# Revit family: Zumtobel MELLOW LIGHT 6 inf - EB
name_source: partatom
category: Lighting Fixtures
revit_build: Autodesk Revit 2014 (Build: 20140709_2115(x64)
units: mm (PartAtom-declared; Revit-internal decimal feet)

## types (12) — shared parameters
Assembly Code = D5020200
Body = Zumtobel_Metal_White
Color Filter = 16777215
Cover = Zumtobel_Metal_Aluminium
Description = Mellow light recessed luminaire
Dimming Lamp Color Temperature Shift = <None>
Emit Shape Visible in Rendering = No
Lamp = LED
Manufacturer = Zumtobel Lighting
Tilt Angle = 90.00°
Voltage = 230 V
Wings = Zumtobel_PMMA_White
zero-valued in all types: Default Elevation

## per-type parameters (varying)
| type | Apparent Load | Emit from Rectangle Length | Emit from Rectangle Width | Height | Length | Middle Part | Model | Photometric Web File | URL | Width |
| ML inf EL LED3600 M625 Q | 33 VA | 599 mm | 599 mm | 77 mm  [stored 0.252625 ft] | 623 mm  [stored 2.04396 ft] | Zumtobel_PMMA_White | 42185201 | D37856AA_MLinf_EL_LED3600-840_M625Q_complete.ies | http://www.zumtobel.com
42184948 | 623 mm  [stored 2.04396 ft] |
| ML inf EL LED3600 M625 L | 33 VA | 1224 mm  [stored 4.01575 ft] | 286 mm  [stored 0.93832 ft] | 82 mm  [stored 0.269029 ft] | 1248 mm  [stored 4.09449 ft] | Zumtobel_PMMA_White | 42185202 | D37805AA_MLinf_EL_LED3600-840_M625L12_complete.ies | http://www.zumtobel.com
42184948 | 310 mm  [stored 1.01706 ft] |
| ML inf EL LED3600 M600 Q | 33 VA | 574 mm  [stored 1.8832 ft] | 574 mm  [stored 1.8832 ft] | 77 mm  [stored 0.252625 ft] | 598 mm  [stored 1.96194 ft] | Zumtobel_PMMA_White | 42184770 | D37856AA_MLinf_EL_LED3600-840_M600Q_complete.ies | http://www.zumtobel.com
42184948 | 598 mm  [stored 1.96194 ft] |
| ML inf EL LED3600 M600 L | 34 VA | 1174 mm  [stored 3.85171 ft] | 274 mm  [stored 0.89895 ft] | 82 mm  [stored 0.269029 ft] | 1198 mm  [stored 3.93045 ft] | Zumtobel_PMMA_White | 42184954 | D37805AA_MLinf_EL_LED3600-840_M600L12_complete.ies | http://www.zumtobel.com
42184948 | 298 mm  [stored 0.97769 ft] |
| ML inf EA LED4800 M625 Q | 49 VA | 599 mm | 599 mm | 77 mm  [stored 0.252625 ft] | 623 mm  [stored 2.04396 ft] | Zumtobel_PMMA_White_Diffusor | 42184948 | D37852AA_MLinf_EA_LED4800-840_M625Q_complete.ies | http://www.zumtobel.com
42184948 | 623 mm  [stored 2.04396 ft] |
| ML inf EA LED4800 M625 L | 50 VA | 1224 mm  [stored 4.01575 ft] | 286 mm  [stored 0.93832 ft] | 82 mm  [stored 0.269029 ft] | 1248 mm  [stored 4.09449 ft] | Zumtobel_PMMA_White_Diffusor | 42184949 | D37773AA_MLinf_EA_LED4800-840_M625L12_complete.ies | http://www.zumtobel.com
42182682 | 310 mm  [stored 1.01706 ft] |
| ML inf EA LED4800 M600 Q | 51 VA | 574 mm  [stored 1.8832 ft] | 574 mm  [stored 1.8832 ft] | 77 mm  [stored 0.252625 ft] | 598 mm  [stored 1.96194 ft] | Zumtobel_PMMA_White_Diffusor | 42184769 | D37852AA_MLinf_EA_LED4800-840_M600Q_complete.ies | http://www.zumtobel.com
42182682 | 598 mm  [stored 1.96194 ft] |
| ML inf EA LED4800 M600 L | 50 VA | 1174 mm  [stored 3.85171 ft] | 274 mm  [stored 0.89895 ft] | 82 mm  [stored 0.269029 ft] | 1198 mm  [stored 3.93045 ft] | Zumtobel_PMMA_White_Diffusor | 42184947 | D37773AA_MLinf_EA_LED4800-840_M600L12_complete.ies | http://www.zumtobel.com
42182682 | 298 mm  [stored 0.97769 ft] |
| ML inf EA LED3600 M625 Q | 36 VA | 599 mm | 599 mm | 77 mm  [stored 0.252625 ft] | 623 mm  [stored 2.04396 ft] | Zumtobel_PMMA_White_Diffusor | 42185193 | D37852AA_MLinf_EA_LED3600-840_M625Q_complete.ies | http://www.zumtobel.com
42182682 | 623 mm  [stored 2.04396 ft] |
| ML inf EA LED3600 M625 L | 36 VA | 1224 mm  [stored 4.01575 ft] | 286 mm  [stored 0.93832 ft] | 82 mm  [stored 0.269029 ft] | 1248 mm  [stored 4.09449 ft] | Zumtobel_PMMA_White_Diffusor | 42185194 | D37773AA_MLinf_EA_LED3600-840_M625L12_complete.ies | http://www.zumtobel.com
42182682 | 310 mm  [stored 1.01706 ft] |
| ML inf EA LED3600 M600 Q | 36 VA | 574 mm  [stored 1.8832 ft] | 574 mm  [stored 1.8832 ft] | 77 mm  [stored 0.252625 ft] | 598 mm  [stored 1.96194 ft] | Zumtobel_PMMA_White_Diffusor | 42185191 | D37852AA_MLinf_EA_LED3600-840_M600Q_complete.ies | http://www.zumtobel.com
42182682 | 598 mm  [stored 1.96194 ft] |
| ML inf EA LED3600 M600 L | 36 VA | 1174 mm  [stored 3.85171 ft] | 274 mm  [stored 0.89895 ft] | 82 mm  [stored 0.269029 ft] | 1198 mm  [stored 3.93045 ft] | Zumtobel_PMMA_White_Diffusor | 42185192 | D37773AA_MLinf_EA_LED3600-840_M600L12_complete.ies | http://www.zumtobel.com
42182682 | 298 mm  [stored 0.97769 ft] |

note: [stored X ft] marks values corroborated as IEEE doubles in the binary element streams (Revit-internal decimal feet)

## geometry (parser evidence)
native form markers: Sweep x4
no freeform markers — native parametric forms only
